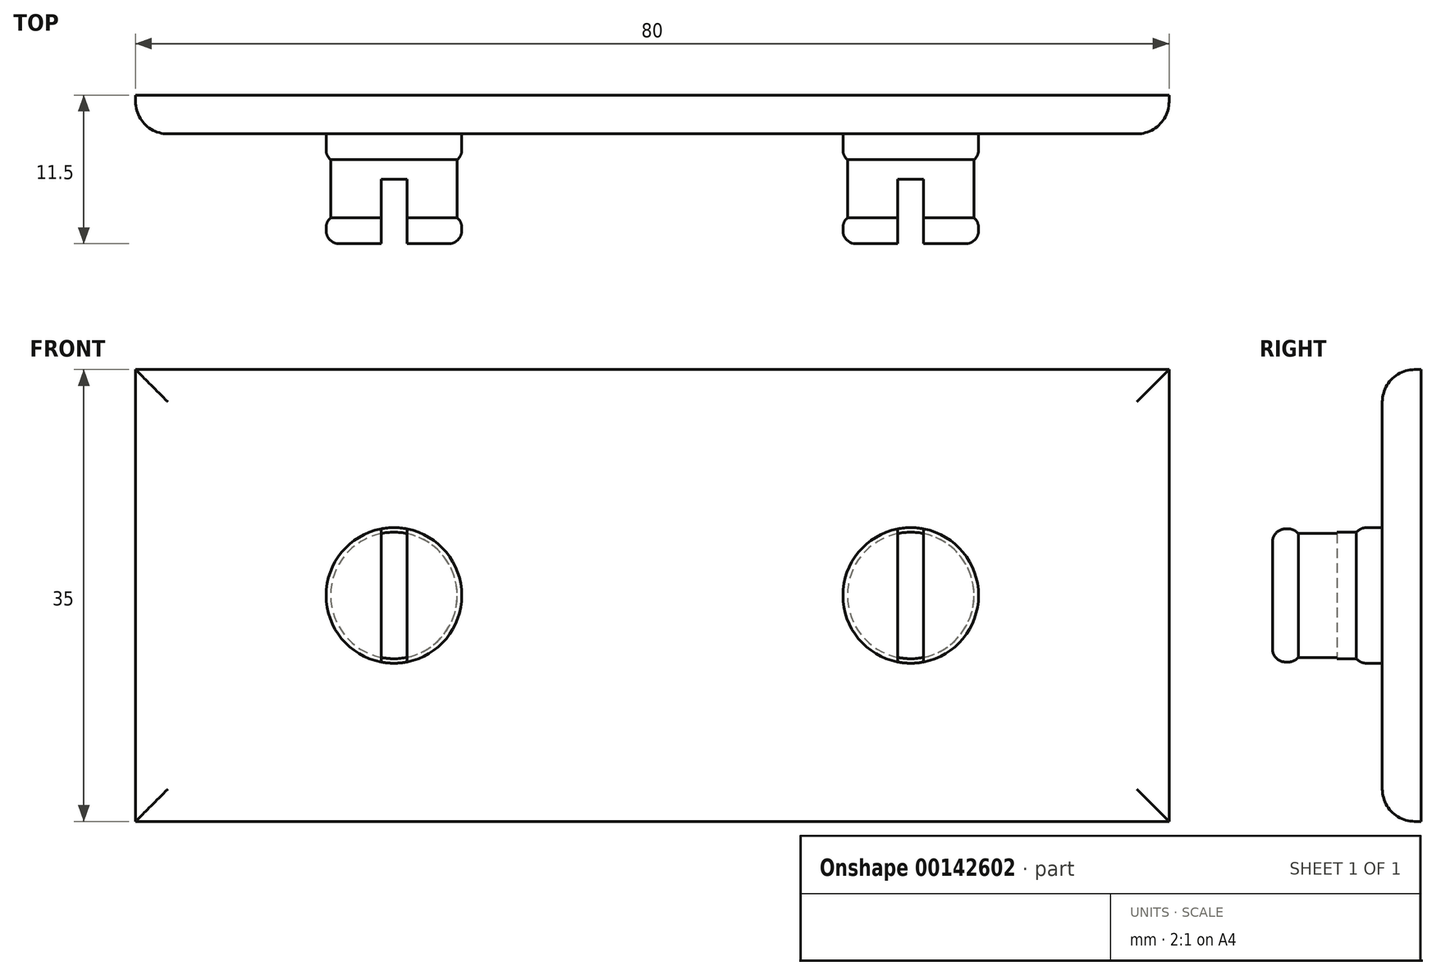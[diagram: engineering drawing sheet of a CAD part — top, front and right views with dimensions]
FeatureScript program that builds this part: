
annotation { "Feature Type Name" : "Feature", "Feature Type Description" : "" }
export const myFeature = defineFeature(function(context is Context, id is Id, definition is map)
    precondition{}
    {
        {
            var Q0;
            Q0=qCreatedBy(makeId("Front.planeOp"),FACE);
            var sketch = newSketch(context, id + "F0", { "sketchPlane" : qUnion([Q0])});
            skLineSegment(sketch, "E0.bottom", {"start": v(40, -17.5) * mm, "end": v(-40, -17.5) * mm});
            skLineSegment(sketch, "E0.top", {"start": v(40, 17.5) * mm, "end": v(-40, 17.5) * mm});
            skLineSegment(sketch, "E0.left", {"start": v(40, -17.5) * mm, "end": v(40, 17.5) * mm});
            skLineSegment(sketch, "E0.right", {"start": v(-40, -17.5) * mm, "end": v(-40, 17.5) * mm});
            skPoint(sketch, "E0.middle", {"position": v(0, 0) * mm});
            skSolve(sketch);
        }
        {
            var Q0;
            Q0=makeQuery(id+"F0.imprint","IMPRINT",FACE,{"disambiguationData":[TD([[makeQuery(id+"F0.imprint","IMPRINT",EDGE,{"derivedFrom":sQuery(id+"F0.wireOp",EDGE,"E0.bottom")}),-1.0]])]});
            extrude(context, id + "F1", {"entities" : qUnion([Q0]), "depth" : 3 * mm});
        }
        {
            var Q0;
            Q0=makeQuery(id+"F1.opExtrude","CAP_FACE",FACE,{"disambiguationData":[OSD([sQuery(id+"F0.wireOp",EDGE,"E0.bottom"),sQuery(id+"F0.wireOp",EDGE,"E0.top"),sQuery(id+"F0.wireOp",EDGE,"E0.left"),sQuery(id+"F0.wireOp",EDGE,"E0.right")])],"isStart":false});
            var sketch = newSketch(context, id + "F2", { "sketchPlane" : qUnion([Q0])});
            skLineSegment(sketch, "E1", {"start": v(0, 0) * mm, "end": v(0, 451.8) * mm, "construction": true});
            skCircle(sketch, "E2", {"center": v(-20, 0) * mm, "radius": 5.25 * mm});
            skCircle(sketch, "E3.MirrorC", {"center": v(20, 0) * mm, "radius": 5.25 * mm});
            skSolve(sketch);
        }
        {
            var Q0;
            Q0=qSketchRegion(id+"F2",true);
            extrude(context, id + "F3", {"entities" : qUnion([Q0]), "operationType" : NewBodyOperationType.ADD, "depth" : 2 * mm});
        }
        {
            var Q0;
            Q0=makeQuery(id+"F3.opExtrude","CAP_FACE",FACE,{"disambiguationData":[OSD([sQuery(id+"F2.wireOp",EDGE,"E2")])],"isStart":false});
            var sketch = newSketch(context, id + "F4", { "sketchPlane" : qUnion([Q0])});
            skLineSegment(sketch, "E4", {"start": v(0, 0) * mm, "end": v(0, 13.5) * mm, "construction": true});
            skCircle(sketch, "E5", {"center": v(-20, 0) * mm, "radius": 4.9 * mm});
            skCircle(sketch, "E6.MirrorC", {"center": v(20, 0) * mm, "radius": 4.9 * mm});
            skSolve(sketch);
        }
        {
            var Q0;
            Q0=qSketchRegion(id+"F4",true);
            extrude(context, id + "F5", {"entities" : qUnion([Q0]), "operationType" : NewBodyOperationType.ADD, "depth" : 4.5 * mm});
        }
        {
            var Q0;
            Q0=makeQuery(id+"F5.opExtrude","CAP_FACE",FACE,{"disambiguationData":[OSD([sQuery(id+"F4.wireOp",EDGE,"E5")])],"isStart":false});
            var sketch = newSketch(context, id + "F6", { "sketchPlane" : qUnion([Q0])});
            skLineSegment(sketch, "E7", {"start": v(0, 0) * mm, "end": v(0, 11.92) * mm, "construction": true});
            skCircle(sketch, "E8", {"center": v(-20, 0) * mm, "radius": 5.25 * mm});
            skCircle(sketch, "E9.MirrorC", {"center": v(20, 0) * mm, "radius": 5.25 * mm});
            skSolve(sketch);
        }
        {
            var Q0;
            Q0=qSketchRegion(id+"F6",true);
            extrude(context, id + "F7", {"entities" : qUnion([Q0]), "operationType" : NewBodyOperationType.ADD, "depth" : 2 * mm});
        }
        {
            var Q0;
            Q0=makeQuery(id+"F3.opExtrude","CAP_EDGE",EDGE,{"disambiguationData":[OSD([sQuery(id+"F2.wireOp",EDGE,"E2")])],"isStart":true});
            var Q1;
            Q1=makeQuery(id+"F3.opExtrude","CAP_EDGE",EDGE,{"disambiguationData":[OSD([sQuery(id+"F2.wireOp",EDGE,"E2")])],"isStart":false});
            var Q2;
            Q2=makeQuery(id+"F7.opExtrude","CAP_EDGE",EDGE,{"disambiguationData":[OSD([sQuery(id+"F6.wireOp",EDGE,"E8")])],"isStart":true});
            var Q3;
            Q3=makeQuery(id+"F7.opExtrude","CAP_EDGE",EDGE,{"disambiguationData":[OSD([sQuery(id+"F6.wireOp",EDGE,"E8")])],"isStart":false});
            var Q4;
            Q4=makeQuery(id+"F3.opExtrude","CAP_EDGE",EDGE,{"disambiguationData":[OSD([sQuery(id+"F2.wireOp",EDGE,"E3.MirrorC")])],"isStart":true});
            var Q5;
            Q5=makeQuery(id+"F3.opExtrude","CAP_EDGE",EDGE,{"disambiguationData":[OSD([sQuery(id+"F2.wireOp",EDGE,"E3.MirrorC")])],"isStart":false});
            var Q6;
            Q6=makeQuery(id+"F7.opExtrude","CAP_EDGE",EDGE,{"disambiguationData":[OSD([sQuery(id+"F6.wireOp",EDGE,"E9.MirrorC")])],"isStart":true});
            var Q7;
            Q7=makeQuery(id+"F7.opExtrude","CAP_EDGE",EDGE,{"disambiguationData":[OSD([sQuery(id+"F6.wireOp",EDGE,"E9.MirrorC")])],"isStart":false});
            fillet(context, id + "F8", {"entities" : qUnion([Q0, Q1, Q2, Q3, Q4, Q5, Q6, Q7]), "radius" : 1 * mm, "tangentPropagation" : true, "allowEdgeOverflow" : false});
        }
        {
            var Q0;
            Q0=makeQuery(id+"F7.opExtrude","CAP_FACE",FACE,{"disambiguationData":[OSD([sQuery(id+"F6.wireOp",EDGE,"E8")])],"isStart":false});
            var sketch = newSketch(context, id + "F9", { "sketchPlane" : qUnion([Q0])});
            skLineSegment(sketch, "E10", {"start": v(0, 0) * mm, "end": v(0, 10.36) * mm, "construction": true});
            skLineSegment(sketch, "E11.bottom", {"start": v(-21, 7.5) * mm, "end": v(-19, 7.5) * mm});
            skLineSegment(sketch, "E11.top", {"start": v(-21, -7.5) * mm, "end": v(-19, -7.5) * mm});
            skLineSegment(sketch, "E11.left", {"start": v(-21, 7.5) * mm, "end": v(-21, -7.5) * mm});
            skLineSegment(sketch, "E11.right", {"start": v(-19, 7.5) * mm, "end": v(-19, -7.5) * mm});
            skPoint(sketch, "E11.middle", {"position": v(-20, 0) * mm});
            skLineSegment(sketch, "E12.MirrorCS", {"start": v(19, 7.5) * mm, "end": v(19, -7.5) * mm});
            skLineSegment(sketch, "E13.MirrorCS", {"start": v(21, 7.5) * mm, "end": v(19, 7.5) * mm});
            skLineSegment(sketch, "E14.MirrorCS", {"start": v(21, 7.5) * mm, "end": v(21, -7.5) * mm});
            skLineSegment(sketch, "E15.MirrorCS", {"start": v(21, -7.5) * mm, "end": v(19, -7.5) * mm});
            skSolve(sketch);
        }
        {
            var Q0;
            Q0=qSketchRegion(id+"F9",true);
            extrude(context, id + "F10", {"entities" : qUnion([Q0]), "operationType" : NewBodyOperationType.REMOVE, "oppositeDirection" : true, "depth" : 5 * mm});
        }
        {
            var Q0;
            Q0=makeQuery(id+"F1.opExtrude","CAP_EDGE",EDGE,{"disambiguationData":[OSD([sQuery(id+"F0.wireOp",EDGE,"E0.right")])],"isStart":false});
            var Q1;
            Q1=makeQuery(id+"F1.opExtrude","CAP_EDGE",EDGE,{"disambiguationData":[OSD([sQuery(id+"F0.wireOp",EDGE,"E0.top")])],"isStart":false});
            var Q2;
            Q2=makeQuery(id+"F1.opExtrude","CAP_EDGE",EDGE,{"disambiguationData":[OSD([sQuery(id+"F0.wireOp",EDGE,"E0.left")])],"isStart":false});
            var Q3;
            Q3=makeQuery(id+"F1.opExtrude","CAP_EDGE",EDGE,{"disambiguationData":[OSD([sQuery(id+"F0.wireOp",EDGE,"E0.bottom")])],"isStart":false});
            fillet(context, id + "F11", {"entities" : qUnion([Q0, Q1, Q2, Q3]), "radius" : 2.5 * mm, "tangentPropagation" : true, "allowEdgeOverflow" : false});
        }
    });
